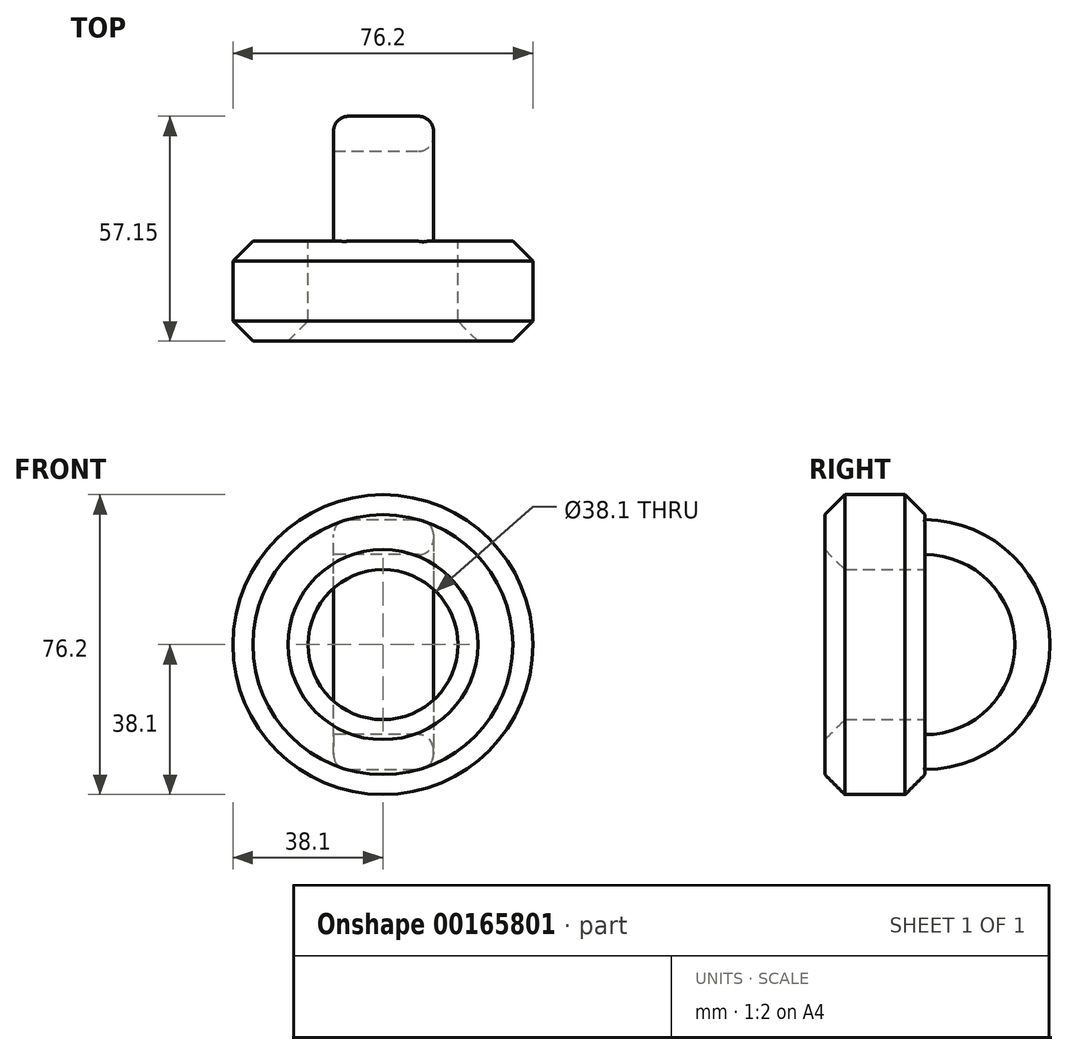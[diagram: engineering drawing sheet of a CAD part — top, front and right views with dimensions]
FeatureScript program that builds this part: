
annotation { "Feature Type Name" : "Feature", "Feature Type Description" : "" }
export const myFeature = defineFeature(function(context is Context, id is Id, definition is map)
    precondition{}
    {
        {
            var Q0;
            Q0=qCreatedBy(makeId("Front.planeOp"),FACE);
            var sketch = newSketch(context, id + "F0", { "sketchPlane" : qUnion([Q0])});
            skCircle(sketch, "E0", {"center": v(0, 0) * mm, "radius": 38.1 * mm});
            skCircle(sketch, "E1", {"center": v(0, 0) * mm, "radius": 19.05 * mm});
            skSolve(sketch);
        }
        {
            var Q0;
            Q0 = qSketchRegion(id + "F0", true);
            extrude(context, id + "F1", {"entities" : qUnion([Q0]), "depth" : 25.4 * mm});
        }
        {
            var Q0;
            Q0=qCreatedBy(makeId("Front.planeOp"),FACE);
            var sketch = newSketch(context, id + "F2", { "sketchPlane" : qUnion([Q0])});
            skLineSegment(sketch, "E2", {"start": v(-55.1, 0) * mm, "end": v(-55.1, 22.86) * mm});
            skLineSegment(sketch, "E3", {"start": v(-55.1, 22.86) * mm, "end": v(-55.1, 31.75) * mm});
            skLineSegment(sketch, "E4", {"start": v(12.84, 22.86) * mm, "end": v(-12.55, 22.86) * mm});
            skLineSegment(sketch, "E5", {"start": v(0, 32.09) * mm, "end": v(-12.55, 31.75) * mm});
            skPoint(sketch, "E6.end.orphan", {"position": v(12.84, 31.75) * mm});
            skLineSegment(sketch, "E7", {"start": v(-12.55, 31.75) * mm, "end": v(12.84, 31.75) * mm});
            skLineSegment(sketch, "E8", {"start": v(12.84, 31.75) * mm, "end": v(12.84, 22.86) * mm});
            skLineSegment(sketch, "E9", {"start": v(-12.55, 22.86) * mm, "end": v(-12.55, 31.75) * mm});
            skLineSegment(sketch, "E10.top", {"start": v(-12.55, 22.86) * mm, "end": v(12.84, 22.86) * mm});
            skLineSegment(sketch, "E10.left", {"start": v(-12.55, 31.75) * mm, "end": v(-12.55, 22.86) * mm});
            skLineSegment(sketch, "E11", {"start": v(-12.55, 31.75) * mm, "end": v(-12.55, 56.9) * mm});
            skLineSegment(sketch, "E12", {"start": v(12.84, 31.75) * mm, "end": v(12.84, 57.48) * mm});
            skLineSegment(sketch, "E13", {"start": v(0.14, 27.53) * mm, "end": v(0.14, 55.48) * mm});
            skPoint(sketch, "E13.startSnap0", {"position": v(0.14, 22.86) * mm});
            skLineSegment(sketch, "E14", {"start": v(-46.2, 0) * mm, "end": v(62.75, 0) * mm});
            skSolve(sketch);
        }
        {
            var Q0;
            Q0 = qSketchRegion(id + "F2", true);
            var Q1;
            Q1=sQuery(id+"F2.wireOp",EDGE,"E14");
            revolve(context, id + "F3", {"operationType" : NewBodyOperationType.ADD, "entities" : qUnion([Q0]), "axis" : qUnion([Q1]), "revolveType" : RevolveType.ONE_DIRECTION, "oppositeDirection" : true, "angle" : 180 * degree});
        }
        {
            var Q0;
            Q0=makeQuery(id+"F3.opRevolve","SWEPT_EDGE",EDGE,{"disambiguationData":[OSD([sQuery(id+"F2.wireOp",EDGE,"E7"),sQuery(id+"F2.wireOp",EDGE,"E8")])]});
            var Q1;
            Q1=makeQuery(id+"F3.opRevolve","SWEPT_EDGE",EDGE,{"disambiguationData":[OSD([sQuery(id+"F2.wireOp",EDGE,"E7"),sQuery(id+"F2.wireOp",EDGE,"E10.left")])]});
            var Q2;
            Q2=makeQuery(id+"F3.opRevolve","SWEPT_EDGE",EDGE,{"disambiguationData":[OSD([sQuery(id+"F2.wireOp",EDGE,"E10.top"),sQuery(id+"F2.wireOp",EDGE,"E10.left")])]});
            var Q3;
            Q3=makeQuery(id+"F3.opRevolve","SWEPT_EDGE",EDGE,{"disambiguationData":[OSD([sQuery(id+"F2.wireOp",EDGE,"E10.top"),sQuery(id+"F2.wireOp",EDGE,"E8")])]});
            fillet(context, id + "F4", {"entities" : qUnion([Q0, Q1, Q2, Q3]), "radius" : 3.8 * mm, "tangentPropagation" : true, "allowEdgeOverflow" : false});
        }
        {
            var Q0;
            Q0=makeQuery(id+"F1.opExtrude","CAP_EDGE",EDGE,{"disambiguationData":[OSD([sQuery(id+"F0.wireOp",EDGE,"E0")])],"isStart":true});
            var Q1;
            Q1=makeQuery(id+"F1.opExtrude","CAP_FACE",FACE,{"disambiguationData":[OSD([sQuery(id+"F0.wireOp",EDGE,"E0"),sQuery(id+"F0.wireOp",EDGE,"E1")])],"isStart":false});
            chamfer(context, id + "F5", {"entities" : qUnion([Q0, Q1]), "width" : 5.08 * mm, "tangentPropagation" : true});
        }
    });
